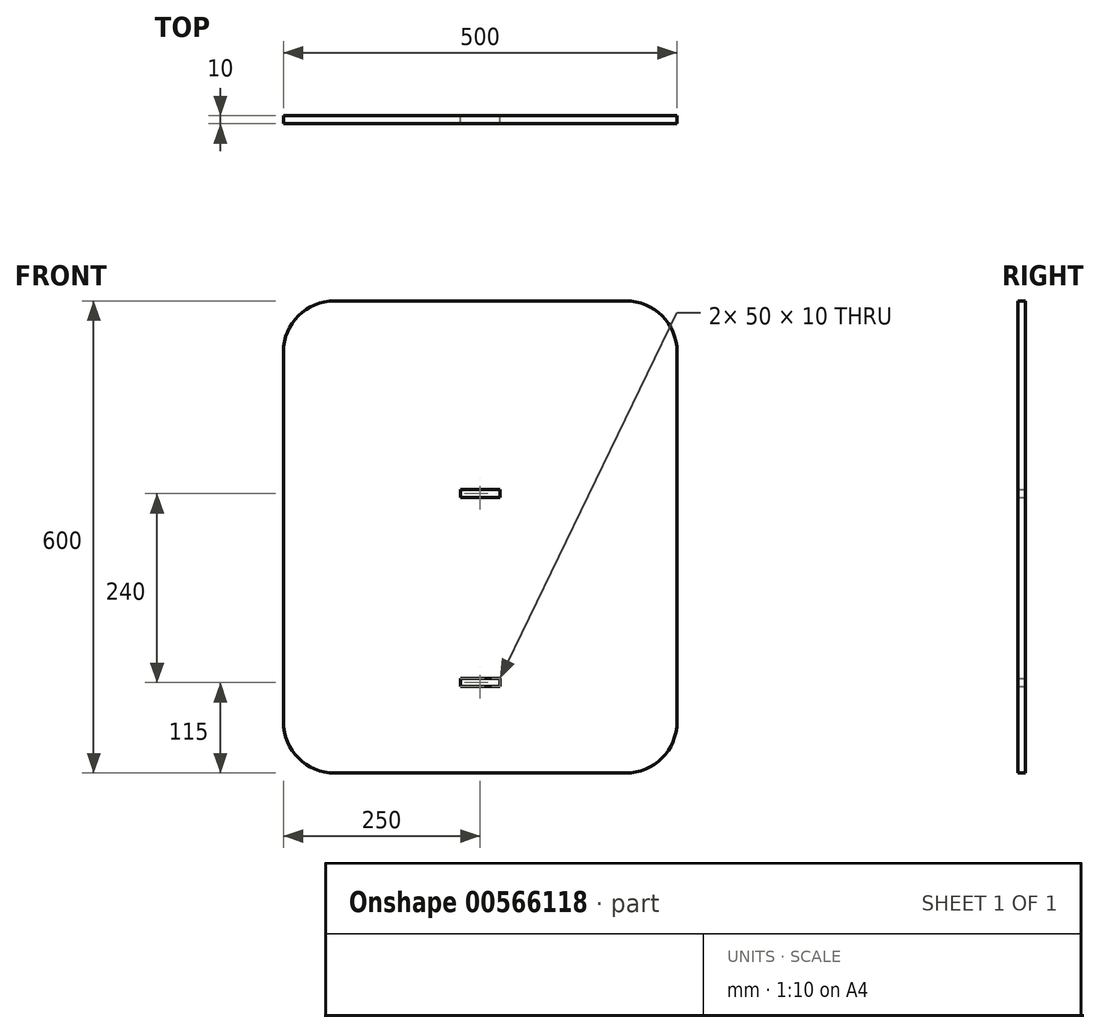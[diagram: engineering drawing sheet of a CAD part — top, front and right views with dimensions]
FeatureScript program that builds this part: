
annotation { "Feature Type Name" : "Feature", "Feature Type Description" : "" }
export const myFeature = defineFeature(function(context is Context, id is Id, definition is map)
    precondition{}
    {
        {
            var Q0;
            Q0=qCreatedBy(makeId("Front.planeOp"),FACE);
            var sketch = newSketch(context, id + "F0", { "sketchPlane" : qUnion([Q0])});
            skLineSegment(sketch, "E0.bottom", {"start": v(-185, 300) * mm, "end": v(185, 300) * mm});
            skLineSegment(sketch, "E0.top", {"start": v(-185, -300) * mm, "end": v(185, -300) * mm});
            skLineSegment(sketch, "E0.left", {"start": v(-250, 235) * mm, "end": v(-250, -235) * mm});
            skLineSegment(sketch, "E0.right", {"start": v(250, 235) * mm, "end": v(250, -235) * mm});
            skPoint(sketch, "E0.middle", {"position": v(0, 0) * mm});
            skPoint(sketch, "E1.visualSharp", {"position": v(-250, 300) * mm});
            skArc(sketch, "E1.filletArc", {"start": v(-185, 300) * mm, "mid": v(-230.96, 280.96) * mm, "end": v(-250, 235) * mm});
            skPoint(sketch, "E2.visualSharp", {"position": v(250, 300) * mm});
            skArc(sketch, "E2.filletArc", {"start": v(250, 235) * mm, "mid": v(230.96, 280.96) * mm, "end": v(185, 300) * mm});
            skPoint(sketch, "E3.visualSharp", {"position": v(250, -300) * mm});
            skArc(sketch, "E3.filletArc", {"start": v(185, -300) * mm, "mid": v(230.96, -280.96) * mm, "end": v(250, -235) * mm});
            skPoint(sketch, "E4.visualSharp", {"position": v(-250, -300) * mm});
            skArc(sketch, "E4.filletArc", {"start": v(-250, -235) * mm, "mid": v(-230.96, -280.96) * mm, "end": v(-185, -300) * mm});
            skLineSegment(sketch, "E5", {"start": v(0, 60) * mm, "end": v(-20, 60) * mm});
            skLineSegment(sketch, "E6", {"start": v(0, 60) * mm, "end": v(20, 60) * mm});
            skLineSegment(sketch, "E7", {"start": v(20, 50) * mm, "end": v(-20, 50) * mm});
            skLineSegment(sketch, "E8", {"start": v(-200, -65) * mm, "end": v(-175, -65) * mm});
            skLineSegment(sketch, "E9", {"start": v(-200, -65) * mm, "end": v(-200, -75) * mm});
            skLineSegment(sketch, "E10", {"start": v(-200, -75) * mm, "end": v(-175, -75) * mm});
            skLineSegment(sketch, "E11", {"start": v(-175, -75) * mm, "end": v(-175, -65) * mm});
            skLineSegment(sketch, "E12", {"start": v(0, -180) * mm, "end": v(-25, -180) * mm});
            skLineSegment(sketch, "E13", {"start": v(0, -180) * mm, "end": v(25, -180) * mm});
            skLineSegment(sketch, "E14", {"start": v(25, -180) * mm, "end": v(25, -190) * mm});
            skLineSegment(sketch, "E15", {"start": v(25, -190) * mm, "end": v(-25, -190) * mm});
            skLineSegment(sketch, "E16", {"start": v(-25, -190) * mm, "end": v(-25, -180) * mm});
            skLineSegment(sketch, "E17", {"start": v(-20, 50) * mm, "end": v(-25, 50) * mm});
            skLineSegment(sketch, "E18", {"start": v(-25, 50) * mm, "end": v(-25, 60) * mm});
            skLineSegment(sketch, "E19", {"start": v(-25, 60) * mm, "end": v(-20, 60) * mm});
            skLineSegment(sketch, "E20", {"start": v(20, 60) * mm, "end": v(25, 60) * mm});
            skLineSegment(sketch, "E21", {"start": v(25, 60) * mm, "end": v(25, 50) * mm});
            skLineSegment(sketch, "E22", {"start": v(25, 50) * mm, "end": v(20, 50) * mm});
            skSolve(sketch);
        }
        {
            var Q0;
            Q0 = qSketchRegion(id + "F0", true);
            var Q1;
            Q1=makeQuery(id+"F0.imprint","IMPRINT",FACE,{"disambiguationData":[TD([[makeQuery(id+"F0.imprint","IMPRINT",EDGE,{"derivedFrom":sQuery(id+"F0.wireOp",EDGE,"E8")}),-1.0]])]});
            extrude(context, id + "F1", {"entities" : qUnion([Q0, Q1]), "depth" : 10 * mm, "offsetDistance" : 25 * mm});
        }
    });
